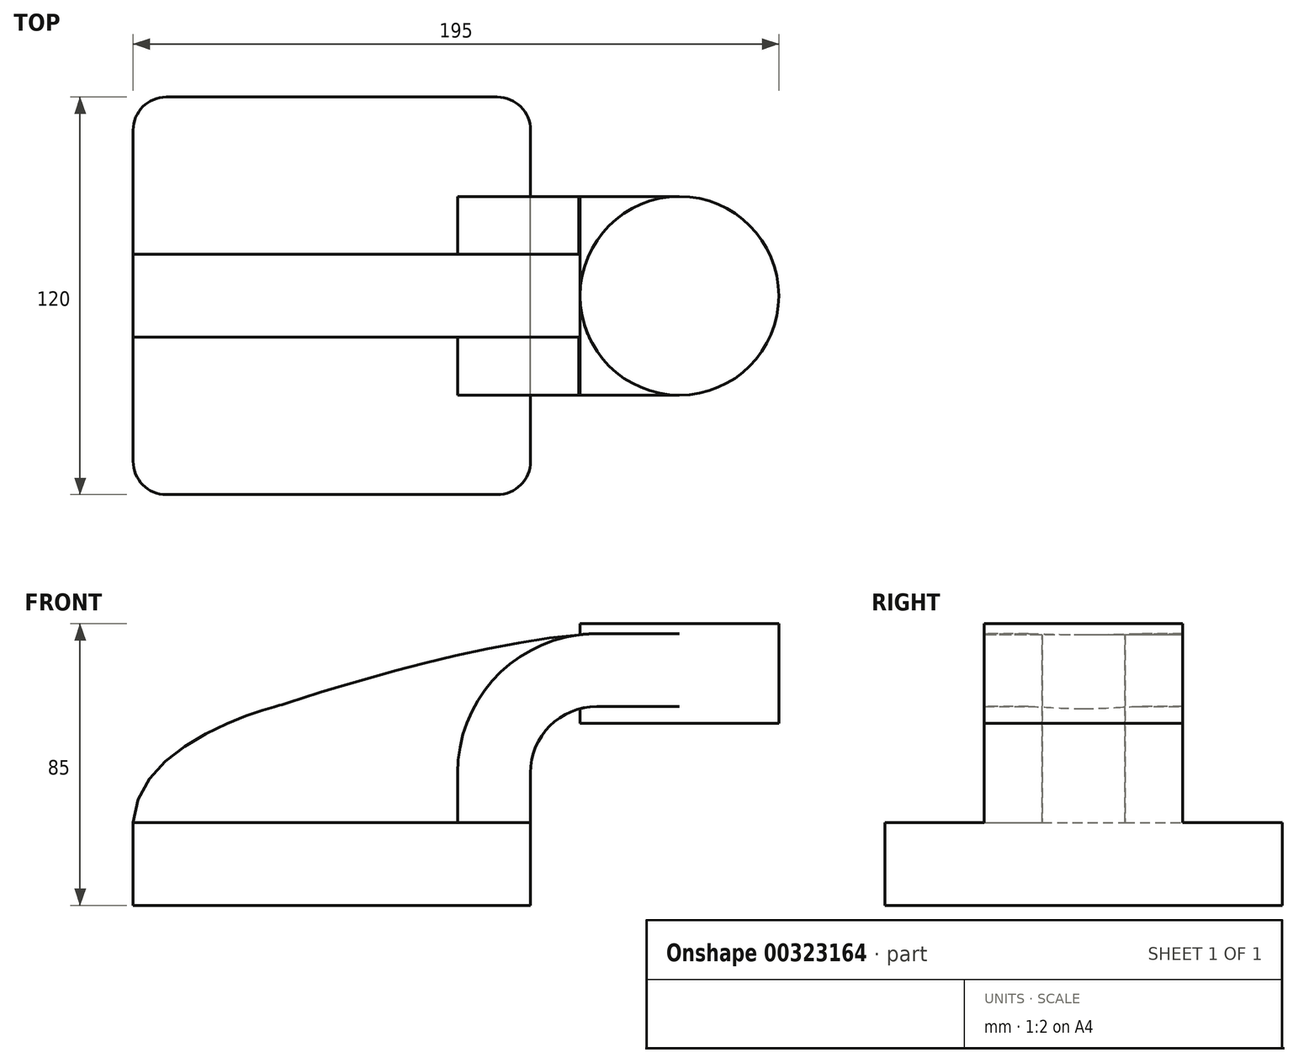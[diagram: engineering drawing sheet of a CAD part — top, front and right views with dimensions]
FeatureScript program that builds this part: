
annotation { "Feature Type Name" : "Feature", "Feature Type Description" : "" }
export const myFeature = defineFeature(function(context is Context, id is Id, definition is map)
    precondition{}
    {
        {
            var Q0;
            Q0=qCreatedBy(makeId("Front.planeOp"),FACE);
            var sketch = newSketch(context, id + "F0", { "sketchPlane" : qUnion([Q0])});
            skLineSegment(sketch, "E0.bottom", {"start": v(-60, -12.5) * mm, "end": v(60, -12.5) * mm});
            skLineSegment(sketch, "E0.top", {"start": v(-60, 12.5) * mm, "end": v(60, 12.5) * mm});
            skLineSegment(sketch, "E0.left", {"start": v(-60, -12.5) * mm, "end": v(-60, 12.5) * mm});
            skLineSegment(sketch, "E0.right", {"start": v(60, -12.5) * mm, "end": v(60, 12.5) * mm});
            skPoint(sketch, "E0.middle", {"position": v(0, 0) * mm});
            skLineSegment(sketch, "E1.bottom", {"start": v(75, 42.5) * mm, "end": v(135, 42.5) * mm});
            skLineSegment(sketch, "E1.top", {"start": v(75, 72.5) * mm, "end": v(135, 72.5) * mm});
            skLineSegment(sketch, "E1.left", {"start": v(75, 42.5) * mm, "end": v(75, 72.5) * mm});
            skLineSegment(sketch, "E1.right", {"start": v(135, 42.5) * mm, "end": v(135, 72.5) * mm});
            skPoint(sketch, "E1.middle", {"position": v(105, 57.5) * mm});
            skLineSegment(sketch, "E2", {"start": v(60, 27.5) * mm, "end": v(60, 12.5) * mm});
            skArc(sketch, "E3", {"start": v(60, 27.5) * mm, "mid": v(65.86, 41.64) * mm, "end": v(80, 47.5) * mm});
            skLineSegment(sketch, "E4", {"start": v(80, 47.5) * mm, "end": v(105, 47.5) * mm});
            skLineSegment(sketch, "E5.0", {"start": v(38, 27.5) * mm, "end": v(38, 12.5) * mm});
            skArc(sketch, "E5.1", {"start": v(38, 27.5) * mm, "mid": v(50.3, 57.2) * mm, "end": v(80, 69.5) * mm});
            skLineSegment(sketch, "E5.2", {"start": v(80, 69.5) * mm, "end": v(105, 69.5) * mm});
            skFitSpline(sketch, "E6", {"points": [v(-60, 12.5) * mm, v(-15.72, 47.85) * mm, v(-15.72, 47.85) * mm, v(80, 69.5) * mm], "startDerivative": vector(8.41, 175.19) * mm, "endDerivative": vector(193.49, 8.3) * mm});
            skLineSegment(sketch, "E7", {"start": v(105, 47.5) * mm, "end": v(105, 69.5) * mm});
            skLineSegment(sketch, "E8", {"start": v(105, 47.5) * mm, "end": v(105, 42.5) * mm});
            skLineSegment(sketch, "E9", {"start": v(105, 42.5) * mm, "end": v(105, 69.5) * mm});
            skLineSegment(sketch, "E10", {"start": v(105, 69.5) * mm, "end": v(105, 72.5) * mm});
            skSolve(sketch);
        }
        {
            var Q0;
            Q0=makeQuery(id+"F0.imprint","IMPRINT",FACE,{"disambiguationData":[TD([[makeQuery(id+"F0.imprint","IMPRINT",EDGE,{"derivedFrom":sQuery(id+"F0.wireOp",EDGE,"E0.bottom")}),1.0]])]});
            extrude(context, id + "F1", {"entities" : qUnion([Q0]), "endBound" : BoundingType.SYMMETRIC, "depth" : 120 * mm});
        }
        {
            var Q0;
            {var subQ1=sQuery(id+"F0.wireOp",EDGE,"E2");Q0=makeQuery(id+"F0.imprint","IMPRINT",FACE,{"disambiguationData":[TD([[makeQuery(id+"F0.imprint","IMPRINT",EDGE,{"derivedFrom":subQ1}),-1.0]])]});}
            var Q1;
            {var subQ0=sQuery(id+"F0.wireOp",EDGE,"E4");var subQ1=sQuery(id+"F0.wireOp",EDGE,"E1.left");var subQ2=makeQuery(id+"F0.imprint","INTERSECT",VERTEX,{"derivedFrom":[subQ1,subQ0]});Q1=makeQuery(id+"F0.imprint","IMPRINT",FACE,{"disambiguationData":[TD([[makeQuery(id+"F0.imprint","IMPRINT",EDGE,{"disambiguationData":[TD([[subQ2,-1.0]])],"derivedFrom":subQ1}),-1.0]])]});}
            var Q2;
            {var subQ1=sQuery(id+"F0.wireOp",EDGE,"E4");Q2=makeQuery(id+"F0.imprint","IMPRINT",FACE,{"disambiguationData":[TD([[makeQuery(id+"F0.imprint","IMPRINT",EDGE,{"derivedFrom":subQ1}),1.0]])]});}
            extrude(context, id + "F2", {"entities" : qUnion([Q0, Q1, Q2]), "operationType" : NewBodyOperationType.ADD, "endBound" : BoundingType.SYMMETRIC, "depth" : 60 * mm});
        }
        {
            var Q0;
            {var subQ3=sQuery(id+"F0.wireOp",EDGE,"E5.0");Q0=makeQuery(id+"F0.imprint","IMPRINT",FACE,{"disambiguationData":[TD([[makeQuery(id+"F0.imprint","IMPRINT",EDGE,{"derivedFrom":subQ3}),-1.0]])]});}
            extrude(context, id + "F3", {"entities" : qUnion([Q0]), "operationType" : NewBodyOperationType.ADD, "endBound" : BoundingType.SYMMETRIC, "depth" : 25 * mm});
        }
        {
            var Q0;
            {var subQ4=sQuery(id+"F0.wireOp",EDGE,"E1.right");Q0=makeQuery(id+"F0.imprint","IMPRINT",FACE,{"disambiguationData":[TD([[makeQuery(id+"F0.imprint","IMPRINT",EDGE,{"derivedFrom":subQ4}),1.0]])]});}
            var Q1;
            Q1=sQuery(id+"F0.wireOp",EDGE,"E7");
            revolve(context, id + "F4", {"operationType" : NewBodyOperationType.ADD, "entities" : qUnion([Q0]), "axis" : qUnion([Q1]), "revolveType" : RevolveType.FULL});
        }
        {
            var Q0;
            Q0=makeQuery(id+"F1.opExtrude","CAP_EDGE",EDGE,{"disambiguationData":[OSD([sQuery(id+"F0.wireOp",EDGE,"E0.left")])],"isStart":false});
            var Q1;
            Q1=makeQuery(id+"F1.opExtrude","CAP_EDGE",EDGE,{"disambiguationData":[OSD([sQuery(id+"F0.wireOp",EDGE,"E0.right")])],"isStart":false});
            var Q2;
            Q2=makeQuery(id+"F1.opExtrude","CAP_EDGE",EDGE,{"disambiguationData":[OSD([sQuery(id+"F0.wireOp",EDGE,"E0.right")])],"isStart":true});
            var Q3;
            Q3=makeQuery(id+"F1.opExtrude","CAP_EDGE",EDGE,{"disambiguationData":[OSD([sQuery(id+"F0.wireOp",EDGE,"E0.left")])],"isStart":true});
            fillet(context, id + "F5", {"entities" : qUnion([Q0, Q1, Q2, Q3]), "radius" : 10 * mm, "tangentPropagation" : true, "allowEdgeOverflow" : false});
        }
    });
